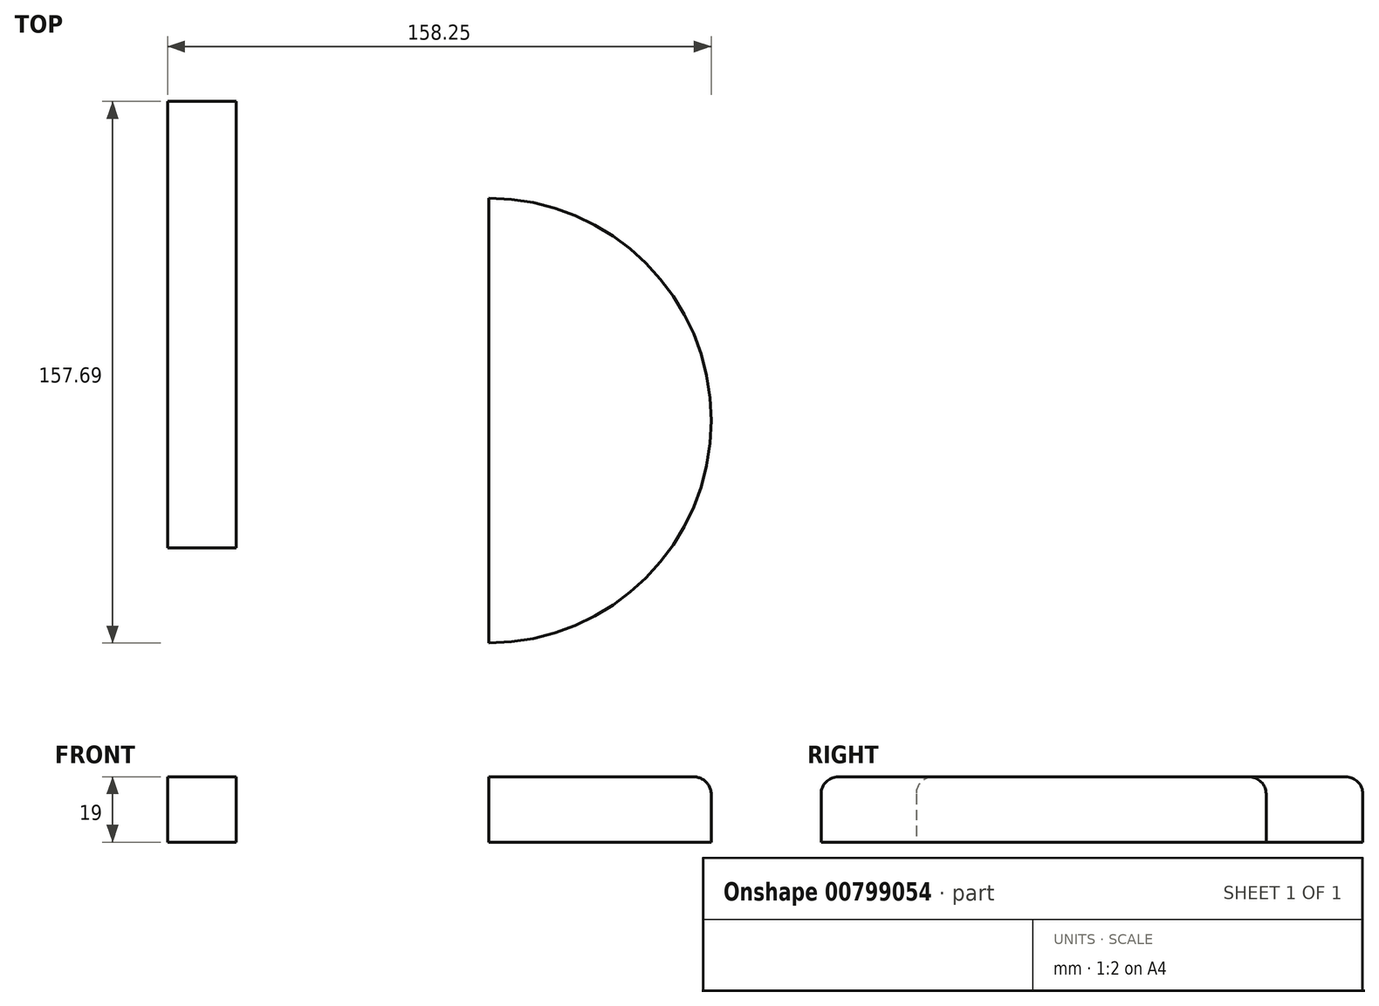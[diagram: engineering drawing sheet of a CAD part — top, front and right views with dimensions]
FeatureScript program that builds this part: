
annotation { "Feature Type Name" : "Feature", "Feature Type Description" : "" }
export const myFeature = defineFeature(function(context is Context, id is Id, definition is map)
    precondition{}
    {
        {
            var Q0;
            Q0=qCreatedBy(makeId("Top.planeOp"),FACE);
            var sketch = newSketch(context, id + "F0", { "sketchPlane" : qUnion([Q0])});
            skLineSegment(sketch, "E0", {"start": v(0, -64.77) * mm, "end": v(0, 64.77) * mm});
            skArc(sketch, "E1", {"start": v(0, -64.77) * mm, "mid": v(64.77, 0) * mm, "end": v(0, 64.77) * mm});
            skSolve(sketch);
        }
        {
            var Q0;
            Q0=makeQuery(id+"F0.imprint","IMPRINT",FACE,{"disambiguationData":[TD([[makeQuery(id+"F0.imprint","IMPRINT",EDGE,{"derivedFrom":sQuery(id+"F0.wireOp",EDGE,"E0")}),-1.0]])]});
            extrude(context, id + "F1", {"entities" : qUnion([Q0]), "depth" : 19 * mm, "offsetDistance" : 25 * mm});
        }
        {
            var Q0;
            Q0=makeQuery(id+"F1.opExtrude","CAP_EDGE",EDGE,{"disambiguationData":[OSD([sQuery(id+"F0.wireOp",EDGE,"E1")])],"isStart":false});
            fillet(context, id + "F2", {"entities" : qUnion([Q0]), "radius" : 5 * mm, "tangentPropagation" : true, "allowEdgeOverflow" : false});
        }
        {
            var Q0;
            Q0=qCreatedBy(makeId("Top.planeOp"),FACE);
            var sketch = newSketch(context, id + "F3", { "sketchPlane" : qUnion([Q0])});
            skLineSegment(sketch, "E2.bottom", {"start": v(-93.48, 92.92) * mm, "end": v(-73.48, 92.92) * mm});
            skLineSegment(sketch, "E2.top", {"start": v(-93.48, -37.08) * mm, "end": v(-73.48, -37.08) * mm});
            skLineSegment(sketch, "E2.left", {"start": v(-93.48, 92.92) * mm, "end": v(-93.48, -37.08) * mm});
            skLineSegment(sketch, "E2.right", {"start": v(-73.48, 92.92) * mm, "end": v(-73.48, -37.08) * mm});
            skSolve(sketch);
        }
        {
            var Q0;
            Q0 = qSketchRegion(id + "F3", true);
            extrude(context, id + "F4", {"entities" : qUnion([Q0]), "depth" : 19 * mm, "offsetDistance" : 25 * mm});
        }
        {
            var Q0;
            Q0=makeQuery(id+"F4.opExtrude","CAP_EDGE",EDGE,{"disambiguationData":[OSD([sQuery(id+"F3.wireOp",EDGE,"E2.top")])],"isStart":false});
            var Q1;
            Q1=makeQuery(id+"F4.opExtrude","CAP_EDGE",EDGE,{"disambiguationData":[OSD([sQuery(id+"F3.wireOp",EDGE,"E2.bottom")])],"isStart":false});
            fillet(context, id + "F5", {"entities" : qUnion([Q0, Q1]), "radius" : 5 * mm, "tangentPropagation" : true, "allowEdgeOverflow" : false});
        }
    });
